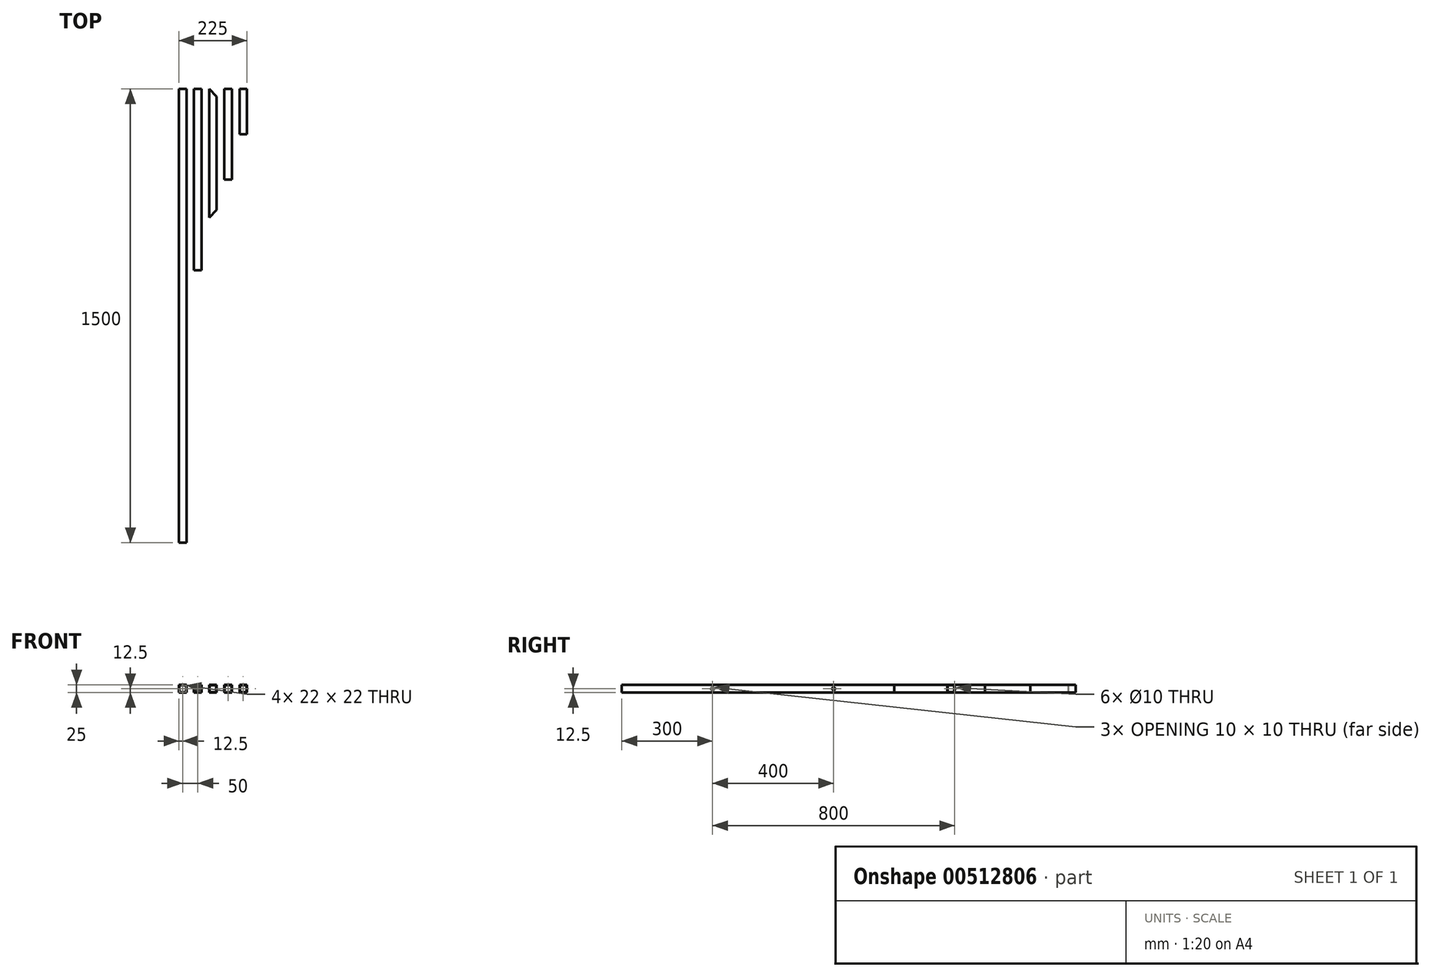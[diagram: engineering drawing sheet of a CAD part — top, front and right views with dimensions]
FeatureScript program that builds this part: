
annotation { "Feature Type Name" : "Feature", "Feature Type Description" : "" }
export const myFeature = defineFeature(function(context is Context, id is Id, definition is map)
    precondition{}
    {
        {
            var Q0;
            Q0=qCreatedBy(makeId("Front.planeOp"),FACE);
            var sketch = newSketch(context, id + "F0", { "sketchPlane" : qUnion([Q0])});
            skLineSegment(sketch, "E0.bottom", {"start": v(12.5, 12.5) * mm, "end": v(-12.5, 12.5) * mm});
            skLineSegment(sketch, "E0.top", {"start": v(12.5, -12.5) * mm, "end": v(-12.5, -12.5) * mm});
            skLineSegment(sketch, "E0.left", {"start": v(12.5, 12.5) * mm, "end": v(12.5, -12.5) * mm});
            skLineSegment(sketch, "E0.right", {"start": v(-12.5, 12.5) * mm, "end": v(-12.5, -12.5) * mm});
            skPoint(sketch, "E0.middle", {"position": v(0, 0) * mm});
            skLineSegment(sketch, "E1.bottom", {"start": v(11, 11) * mm, "end": v(-11, 11) * mm});
            skLineSegment(sketch, "E1.top", {"start": v(11, -11) * mm, "end": v(-11, -11) * mm});
            skLineSegment(sketch, "E1.left", {"start": v(11, 11) * mm, "end": v(11, -11) * mm});
            skLineSegment(sketch, "E1.right", {"start": v(-11, 11) * mm, "end": v(-11, -11) * mm});
            skSolve(sketch);
        }
        {
            var Q0;
            Q0 = qSketchRegion(id + "F0", true);
            extrude(context, id + "F1", {"entities" : qUnion([Q0]), "depth" : 1500 * mm, "offsetDistance" : 25 * mm});
        }
        {
            var Q0;
            Q0=qCreatedBy(makeId("Front.planeOp"),FACE);
            var sketch = newSketch(context, id + "F2", { "sketchPlane" : qUnion([Q0])});
            skPoint(sketch, "E2", {"position": v(50, 0) * mm});
            skLineSegment(sketch, "E3.bottom", {"start": v(62.5, 12.5) * mm, "end": v(37.5, 12.5) * mm});
            skLineSegment(sketch, "E3.top", {"start": v(62.5, -12.5) * mm, "end": v(37.5, -12.5) * mm});
            skLineSegment(sketch, "E3.left", {"start": v(62.5, 12.5) * mm, "end": v(62.5, -12.5) * mm});
            skLineSegment(sketch, "E3.right", {"start": v(37.5, 12.5) * mm, "end": v(37.5, -12.5) * mm});
            skLineSegment(sketch, "E4.bottom", {"start": v(61, 11) * mm, "end": v(39, 11) * mm});
            skLineSegment(sketch, "E4.top", {"start": v(61, -11) * mm, "end": v(39, -11) * mm});
            skLineSegment(sketch, "E4.left", {"start": v(61, 11) * mm, "end": v(61, -11) * mm});
            skLineSegment(sketch, "E4.right", {"start": v(39, 11) * mm, "end": v(39, -11) * mm});
            skSolve(sketch);
        }
        {
            var Q0;
            Q0 = qSketchRegion(id + "F2", true);
            extrude(context, id + "F3", {"entities" : qUnion([Q0]), "depth" : 600 * mm, "offsetDistance" : 25 * mm});
        }
        {
            var Q0;
            Q0=qCreatedBy(makeId("Front.planeOp"),FACE);
            var sketch = newSketch(context, id + "F4", { "sketchPlane" : qUnion([Q0])});
            skPoint(sketch, "E5", {"position": v(100, 0) * mm});
            skLineSegment(sketch, "E6.bottom", {"start": v(112.5, 12.5) * mm, "end": v(87.5, 12.5) * mm});
            skLineSegment(sketch, "E6.top", {"start": v(112.5, -12.5) * mm, "end": v(87.5, -12.5) * mm});
            skLineSegment(sketch, "E6.left", {"start": v(112.5, 12.5) * mm, "end": v(112.5, -12.5) * mm});
            skLineSegment(sketch, "E6.right", {"start": v(87.5, 12.5) * mm, "end": v(87.5, -12.5) * mm});
            skLineSegment(sketch, "E7.bottom", {"start": v(111, 11) * mm, "end": v(89, 11) * mm});
            skLineSegment(sketch, "E7.top", {"start": v(111, -11) * mm, "end": v(89, -11) * mm});
            skLineSegment(sketch, "E7.left", {"start": v(111, 11) * mm, "end": v(111, -11) * mm});
            skLineSegment(sketch, "E7.right", {"start": v(89, 11) * mm, "end": v(89, -11) * mm});
            skSolve(sketch);
        }
        {
            var Q0;
            Q0 = qSketchRegion(id + "F4", true);
            extrude(context, id + "F5", {"entities" : qUnion([Q0]), "depth" : 425 * mm, "offsetDistance" : 25 * mm});
        }
        {
            var Q0;
            Q0=makeQuery(id+"F5.opExtrude","SWEPT_FACE",FACE,{"disambiguationData":[OSD([sQuery(id+"F4.wireOp",EDGE,"E6.bottom")])]});
            var sketch = newSketch(context, id + "F6", { "sketchPlane" : qUnion([Q0])});
            skLineSegment(sketch, "E8.0", {"start": v(112.5, -425) * mm, "end": v(87.5, -425) * mm});
            skPoint(sketch, "E9", {"position": v(112.5, -400) * mm});
            skLineSegment(sketch, "E10", {"start": v(112.5, -400) * mm, "end": v(87.5, -425) * mm});
            skLineSegment(sketch, "E11", {"start": v(112.5, -400) * mm, "end": v(112.5, -425) * mm});
            skLineSegment(sketch, "E12.0", {"start": v(112.5, 0) * mm, "end": v(87.5, 0) * mm});
            skLineSegment(sketch, "E13", {"start": v(112.5, 0) * mm, "end": v(112.5, -25) * mm});
            skLineSegment(sketch, "E14", {"start": v(112.5, -25) * mm, "end": v(87.5, 0) * mm});
            skSolve(sketch);
        }
        {
            var Q0;
            Q0 = qSketchRegion(id + "F6", true);
            extrude(context, id + "F7", {"entities" : qUnion([Q0]), "operationType" : NewBodyOperationType.REMOVE, "oppositeDirection" : true, "depth" : 25 * mm, "offsetDistance" : 25 * mm});
        }
        {
            var Q0;
            Q0=qCreatedBy(makeId("Front.planeOp"),FACE);
            var sketch = newSketch(context, id + "F8", { "sketchPlane" : qUnion([Q0])});
            skPoint(sketch, "E15", {"position": v(150, 0) * mm});
            skLineSegment(sketch, "E16.bottom", {"start": v(162.5, 12.5) * mm, "end": v(137.5, 12.5) * mm});
            skLineSegment(sketch, "E16.top", {"start": v(162.5, -12.5) * mm, "end": v(137.5, -12.5) * mm});
            skLineSegment(sketch, "E16.left", {"start": v(162.5, 12.5) * mm, "end": v(162.5, -12.5) * mm});
            skLineSegment(sketch, "E16.right", {"start": v(137.5, 12.5) * mm, "end": v(137.5, -12.5) * mm});
            skLineSegment(sketch, "E17.bottom", {"start": v(161, 11) * mm, "end": v(139, 11) * mm});
            skLineSegment(sketch, "E17.top", {"start": v(161, -11) * mm, "end": v(139, -11) * mm});
            skLineSegment(sketch, "E17.left", {"start": v(161, 11) * mm, "end": v(161, -11) * mm});
            skLineSegment(sketch, "E17.right", {"start": v(139, 11) * mm, "end": v(139, -11) * mm});
            skSolve(sketch);
        }
        {
            var Q0;
            Q0 = qSketchRegion(id + "F8", true);
            extrude(context, id + "F9", {"entities" : qUnion([Q0]), "depth" : 300 * mm, "offsetDistance" : 25 * mm});
        }
        {
            var Q0;
            Q0=makeQuery(id+"F1.opExtrude","SWEPT_FACE",FACE,{"disambiguationData":[OSD([sQuery(id+"F0.wireOp",EDGE,"E0.right")])]});
            var sketch = newSketch(context, id + "F10", { "sketchPlane" : qUnion([Q0])});
            skPoint(sketch, "E18", {"position": v(400, 0) * mm});
            skPoint(sketch, "E19", {"position": v(800, 0) * mm});
            skPoint(sketch, "E20", {"position": v(1200, 0) * mm});
            skCircle(sketch, "E21", {"center": v(400, 0) * mm, "radius": 5 * mm});
            skCircle(sketch, "E22", {"center": v(800, 0) * mm, "radius": 5 * mm});
            skCircle(sketch, "E23", {"center": v(1200, 0) * mm, "radius": 5 * mm});
            skSolve(sketch);
        }
        {
            var Q0;
            Q0 = qSketchRegion(id + "F10", true);
            extrude(context, id + "F11", {"entities" : qUnion([Q0]), "operationType" : NewBodyOperationType.REMOVE, "oppositeDirection" : true, "depth" : 25 * mm, "offsetDistance" : 25 * mm});
        }
        {
            var Q0;
            Q0=qCreatedBy(makeId("Front.planeOp"),FACE);
            var sketch = newSketch(context, id + "F12", { "sketchPlane" : qUnion([Q0])});
            skPoint(sketch, "E24", {"position": v(200, 0) * mm});
            skLineSegment(sketch, "E25.bottom", {"start": v(187.5, 12.5) * mm, "end": v(212.5, 12.5) * mm});
            skLineSegment(sketch, "E25.top", {"start": v(187.5, -12.5) * mm, "end": v(212.5, -12.5) * mm});
            skLineSegment(sketch, "E25.left", {"start": v(187.5, 12.5) * mm, "end": v(187.5, -12.5) * mm});
            skLineSegment(sketch, "E25.right", {"start": v(212.5, 12.5) * mm, "end": v(212.5, -12.5) * mm});
            skLineSegment(sketch, "E26.bottom", {"start": v(189, 11) * mm, "end": v(211, 11) * mm});
            skLineSegment(sketch, "E26.top", {"start": v(189, -11) * mm, "end": v(211, -11) * mm});
            skLineSegment(sketch, "E26.left", {"start": v(189, 11) * mm, "end": v(189, -11) * mm});
            skLineSegment(sketch, "E26.right", {"start": v(211, 11) * mm, "end": v(211, -11) * mm});
            skSolve(sketch);
        }
        {
            var Q0;
            Q0 = qSketchRegion(id + "F12", true);
            extrude(context, id + "F13", {"entities" : qUnion([Q0]), "depth" : 150 * mm, "offsetDistance" : 25 * mm});
        }
    });
